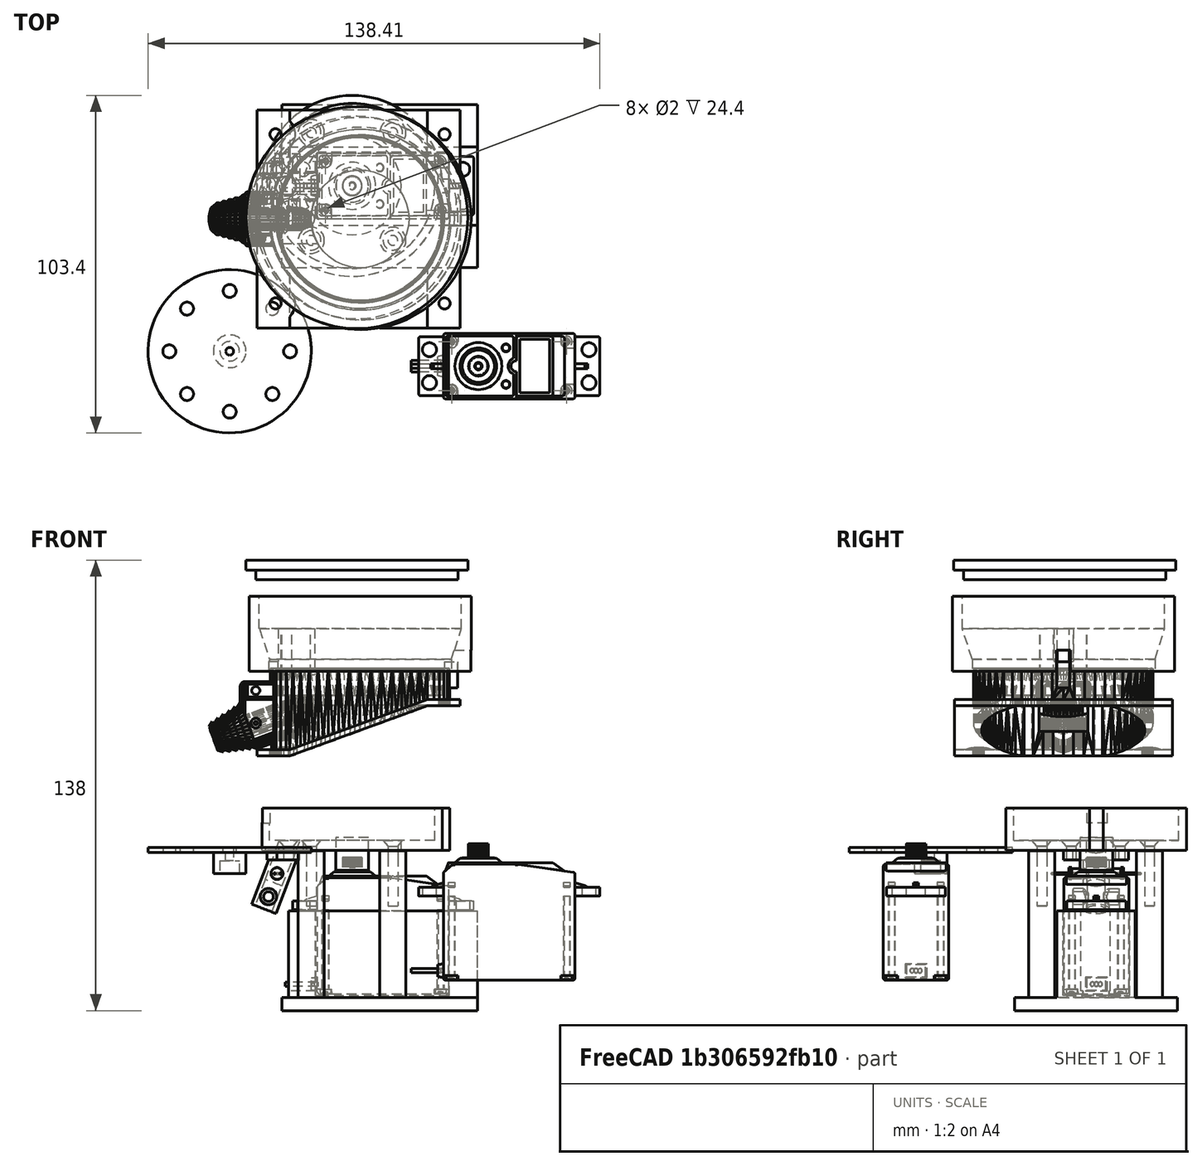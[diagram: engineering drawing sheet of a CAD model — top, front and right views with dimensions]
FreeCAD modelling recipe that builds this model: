
FCSTD DOCUMENT  (FreeCAD 0.21R33694 (Git))
Label: all_parts_chute_with_mount_v6
License: All rights reserved
LicenseURL: http://en.wikipedia.org/wiki/All_rights_reserved
objects: Part::Cylinder×34, Part::Cut×23, Part::MultiFuse×21, Part::Feature×18, Part::Box×11, Part::FeaturePython×5, Part::Cone×2, Sketcher::SketchObject×2, Part::Extrusion×2, Mesh::Feature×1, Part::Fillet×1, Part::Chamfer×1
note: 120 computed .brp shape members not serialized (recipe doc carries the construction recipe); baked Part::Feature solids carry a one-line shape summary decoded from their .brp

FEATURE [Part::Box] Box014  label="Cube014"
  AttacherType = Attacher::AttachEngine3D
  Height = 13
  Length = 4.2
  Placement = pos=(66.2,37.3,63.6) rot=(0,0,1;0rad)
  Width = 4.2
FEATURE [Part::Cylinder] Cylinder022
  Angle = 360
  AttacherType = Attacher::AttachEngine3D
  FirstAngle = 0
  Height = 20
  Placement = pos=(15.5,39.3,51.5) rot=(0,1,0;0.366519rad)
  Radius = 3
  SecondAngle = 0
FEATURE [Part::Box] Box015  label="Cube015"
  AttacherType = Attacher::AttachEngine3D
  Height = 10
  Length = 10
  Placement = pos=(7,36.6,72) rot=(0,0,1;0rad)
  Width = 6.2
FEATURE [Mesh::Feature] Base_V7  label="Base V7"
FEATURE [Part::Feature] Base_V7001_solid  label="hopper (Solid)"
  shape: bbox 76.98 x 66.8 x 28.84 mm, 5900 faces (baked)
FEATURE [Part::Feature] Shape001
  Placement = pos=(47,50.7,-44.8) rot=(0,0,1;3.14159rad)
  shape: bbox 57.75 x 20 x 41.74 mm, 378 faces, 4 solids (baked)
FEATURE [Part::Cylinder] cylinder010  label="servo_central_shaft"
  Angle = 360
  AttacherType = Attacher::AttachEngine3D
  FirstAngle = 0
  Height = 10
  Placement = pos=(37.55,50.7,-7) rot=(0,0,1;0rad)
  Radius = 5
  SecondAngle = 0
FEATURE [Part::Box] Box  label="Cube"
  AttacherType = Attacher::AttachEngine3D
  Height = 27.5
  Length = 58
  Placement = pos=(18,38.6,-47) rot=(0,0,1;0rad)
  Width = 24
FEATURE [Part::Box] Box016  label="Cube016"
  AttacherType = Attacher::AttachEngine3D
  Height = 29.5
  Length = 53
  Placement = pos=(13,46,-44) rot=(0,0,1;0rad)
  Width = 9
FEATURE [Part::Cut] Cut
  Base = -> Box
  Tool = -> Box016
FEATURE [Part::Box] Box017  label="Cube017"
  AttacherType = Attacher::AttachEngine3D
  Height = 29.5
  Length = 10
  Placement = pos=(17,46.6,-46) rot=(0,0,1;0rad)
  Width = 8
FEATURE [Part::Cut] Cut019
  Base = -> Cut
  Tool = -> Box017
FEATURE [Part::Box] Box018  label="Cube018"
  AttacherType = Attacher::AttachEngine3D
  Height = 27.5
  Length = 41
  Placement = pos=(0.5,50.4,-44.2) rot=(0,0,1;0rad)
  Width = 20.4
FEATURE [Part::Fillet] Fillet
  Base = -> Box018
  Edges = 4 edges r=1: [Edge1,Edge3,Edge5,Edge7]
  Placement = pos=(25.85,-9.87885,-1.16822) rot=(0,0,1;0rad)
FEATURE [Part::Cut] Cut020
  Base = -> Cut019
  Tool = -> Fillet
FEATURE [Part::Box] Box020  label="base_plate"
  AttacherType = Attacher::AttachEngine3D
  Height = 4
  Length = 60
  Placement = pos=(16,25.6,-50) rot=(0,0,1;0rad)
  Width = 50
FEATURE [Part::Feature] BOLTS_part  label="Hex socket countersunk head screw M3 20.0"
  Placement = pos=(25,67,2.1) rot=(0,1,0;3.14159rad)
  shape: bbox 6 x 6 x 20 mm, 12 faces (baked)
FEATURE [Part::Feature] BOLTS_part001  label="Hex socket countersunk head screw M3 20.001"
  Placement = pos=(50,67,2.1) rot=(0,1,0;3.14159rad)
  shape: bbox 6 x 6 x 20 mm, 12 faces (baked)
FEATURE [Part::Feature] BOLTS_part002  label="Hex socket countersunk head screw M3 20.002"
  Placement = pos=(50,34,2.1) rot=(0,1,0;3.14159rad)
  shape: bbox 6 x 6 x 20 mm, 12 faces (baked)
FEATURE [Part::Feature] BOLTS_part003  label="Hex socket countersunk head screw M3 20.003"
  Placement = pos=(25,34,2.1) rot=(0,1,0;3.14159rad)
  shape: bbox 6 x 6 x 20 mm, 12 faces (baked)
FEATURE [Part::Cylinder] Cylinder024
  Angle = 360
  AttacherType = Attacher::AttachEngine3D
  FirstAngle = 0
  Height = 48
  Placement = pos=(50,67,-49) rot=(0,0,1;0rad)
  Radius = 4
  SecondAngle = 0
FEATURE [Part::Cylinder] Cylinder025
  Angle = 360
  AttacherType = Attacher::AttachEngine3D
  FirstAngle = 0
  Height = 48
  Placement = pos=(25,34,-49) rot=(0,0,1;0rad)
  Radius = 4
  SecondAngle = 0
FEATURE [Part::Cylinder] Cylinder026
  Angle = 360
  AttacherType = Attacher::AttachEngine3D
  FirstAngle = 0
  Height = 48
  Placement = pos=(25,67,-49) rot=(0,0,1;0rad)
  Radius = 4
  SecondAngle = 0
FEATURE [Part::Cylinder] Cylinder027
  Angle = 360
  AttacherType = Attacher::AttachEngine3D
  FirstAngle = 0
  Height = 48
  Placement = pos=(50,34,-49) rot=(0,0,1;0rad)
  Radius = 4
  SecondAngle = 0
FEATURE [Part::Feature] Shape002  label="led2"
  Placement = pos=(14.5,42.3,-8) rot=(-1,0,0;1.5708rad)
  shape: bbox 3.686 x 11.4 x 3.686 mm, 26 faces, 3 solids (baked)
FEATURE [Part::Feature] Shape003  label="led1"
  Placement = pos=(14.5,59.1,-8) rot=(1,0,0;1.5708rad)
  shape: bbox 3.686 x 11.4 x 3.686 mm, 26 faces, 3 solids (baked)
FEATURE [Part::Feature] BOLTS_part004  label="Hex socket countersunk head screw M3 20.004"
  Placement = pos=(25,34,2.05) rot=(0,1,0;3.14159rad)
  shape: bbox 6 x 6 x 20 mm, 12 faces (baked)
FEATURE [Part::Feature] BOLTS_part005  label="Hex socket countersunk head screw M3 20.005"
  Placement = pos=(50,34,2.05) rot=(0,1,0;3.14159rad)
  shape: bbox 6 x 6 x 20 mm, 12 faces (baked)
FEATURE [Part::Feature] BOLTS_part006  label="Hex socket countersunk head screw M3 20.006"
  Placement = pos=(50,67,2.05) rot=(0,1,0;3.14159rad)
  shape: bbox 6 x 6 x 20 mm, 12 faces (baked)
FEATURE [Part::Feature] BOLTS_part007  label="Hex socket countersunk head screw M3 20.007"
  Placement = pos=(25,67,2.05) rot=(0,1,0;3.14159rad)
  shape: bbox 6 x 6 x 20 mm, 12 faces (baked)
FEATURE [Part::Cylinder] Cylinder032
  Angle = 360
  AttacherType = Attacher::AttachEngine3D
  FirstAngle = 0
  Height = 48
  Placement = pos=(50,67,-43) rot=(0,0,1;0rad)
  Radius = 1.4
  SecondAngle = 0
FEATURE [Part::Cylinder] Cylinder033
  Angle = 360
  AttacherType = Attacher::AttachEngine3D
  FirstAngle = 0
  Height = 48
  Placement = pos=(25,34,-43) rot=(0,0,1;0rad)
  Radius = 1.4
  SecondAngle = 0
FEATURE [Part::Cylinder] Cylinder034
  Angle = 360
  AttacherType = Attacher::AttachEngine3D
  FirstAngle = 0
  Height = 48
  Placement = pos=(25,67,-42) rot=(0,0,1;0rad)
  Radius = 1.4
  SecondAngle = 0
FEATURE [Part::Cylinder] Cylinder035
  Angle = 360
  AttacherType = Attacher::AttachEngine3D
  FirstAngle = 0
  Height = 48
  Placement = pos=(50,34,-43) rot=(0,0,1;0rad)
  Radius = 1.4
  SecondAngle = 0
FEATURE [Part::Cut] Cut030
  Base = -> Cylinder024
  Tool = -> BOLTS_part006
FEATURE [Part::Cut] Cut031
  Base = -> Cylinder025
  Tool = -> BOLTS_part004
FEATURE [Part::Cut] Cut032
  Base = -> Cylinder026
  Tool = -> BOLTS_part007
FEATURE [Part::Cut] Cut033
  Base = -> Cylinder027
  Tool = -> BOLTS_part005
FEATURE [Part::MultiFuse] Fusion011  label="motor_holder"
  Shapes = -> [Cut020,Cut030,Cut031,Cut032,Cut033,Box020]
FEATURE [Part::Cylinder] Cylinder039
  Angle = 360
  AttacherType = Attacher::AttachEngine3D
  FirstAngle = 0
  Height = 21
  Placement = pos=(0,10,4) rot=(1,0,0;1.5708rad)
  Radius = 1.5
  SecondAngle = 0
FEATURE [Part::FeaturePython] Tube003  # WARN: FeaturePython — macro-defined, semantics opaque (R4)
  AttacherType = Attacher::AttachEngine3D
  Height = 5
  InnerRadius = 1.5
  OuterRadius = 2.5
  Placement = pos=(0,2.05,4) rot=(-1,0,0;1.5708rad)
FEATURE [Part::FeaturePython] Tube004  # WARN: FeaturePython — macro-defined, semantics opaque (R4)
  AttacherType = Attacher::AttachEngine3D
  Height = 5
  InnerRadius = 1.5
  OuterRadius = 2.5
  Placement = pos=(0,-2.05,4) rot=(1,0,0;1.5708rad)
FEATURE [Part::Box] Box021  label="Cube019"
  AttacherType = Attacher::AttachEngine3D
  Height = 10
  Length = 20
  Placement = pos=(1.17,-11.94,17.9) rot=(0,0,1;0rad)
  Width = 24
FEATURE [Part::FeaturePython] Tube001  # WARN: FeaturePython — macro-defined, semantics opaque (R4)
  AttacherType = Attacher::AttachEngine3D
  Height = 3
  InnerRadius = 15
  OuterRadius = 27.7
  Placement = pos=(40.45,39.4,63.6) rot=(0,0,1;0rad)
FEATURE [Part::FeaturePython] Tube002  # WARN: FeaturePython — macro-defined, semantics opaque (R4)
  AttacherType = Attacher::AttachEngine3D
  Height = 13
  InnerRadius = 25.3
  OuterRadius = 27.7
  Placement = pos=(40.45,39.4,63.6) rot=(0,0,1;0rad)
FEATURE [Part::MultiFuse] Fusion009
  Shapes = -> [Box014,Tube001,Tube002]
FEATURE [Part::Cut] Cut014  label="cut"
  Base = -> Fusion009
  Tool = -> Cylinder022
FEATURE [Part::Cut] Cut036
  Base = -> Cut014
  Placement = pos=(-2.9,11.3,-64.5) rot=(0,0,1;0rad)
  Tool = -> Box015
FEATURE [Part::MultiFuse] Fusion
  Shapes = -> [BOLTS_part003,Cylinder033]
FEATURE [Part::MultiFuse] Fusion013
  Shapes = -> [BOLTS_part002,Cylinder035]
FEATURE [Part::MultiFuse] Fusion014
  Shapes = -> [BOLTS_part001,Cylinder032]
FEATURE [Part::MultiFuse] Fusion015
  Shapes = -> [BOLTS_part,Cylinder034]
FEATURE [Part::Cut] Cut037
  Base = -> Cut036
  Tool = -> Fusion
FEATURE [Part::Cut] Cut038
  Base = -> Cut037
  Tool = -> Fusion013
FEATURE [Part::Cut] Cut039
  Base = -> Cut038
  Tool = -> Fusion015
FEATURE [Part::Cut] Cut040
  Base = -> Cut039
  Tool = -> Fusion014
FEATURE [Part::Feature] BOLTS_part009  label="Hex socket countersunk head screw M3 20.008"
  Placement = pos=(50,34,2.1) rot=(0,1,0;3.14159rad)
  shape: bbox 6 x 6 x 20 mm, 12 faces (baked)
FEATURE [Part::Cylinder] Cylinder040
  Angle = 360
  AttacherType = Attacher::AttachEngine3D
  FirstAngle = 0
  Height = 48
  Placement = pos=(50,34,-43) rot=(0,0,1;0rad)
  Radius = 1.4
  SecondAngle = 0
FEATURE [Part::MultiFuse] Fusion016
  Placement = pos=(-32,9,0) rot=(0,0,1;0rad)
  Shapes = -> [BOLTS_part009,Cylinder040]
FEATURE [Part::Feature] BOLTS_part010  label="Hex socket countersunk head screw M3 20.009"
  Placement = pos=(50,34,2.1) rot=(0,1,0;3.14159rad)
  shape: bbox 6 x 6 x 20 mm, 12 faces (baked)
FEATURE [Part::Cylinder] Cylinder041
  Angle = 360
  AttacherType = Attacher::AttachEngine3D
  FirstAngle = 0
  Height = 48
  Placement = pos=(50,34,-43) rot=(0,0,1;0rad)
  Radius = 1.4
  SecondAngle = 0
FEATURE [Part::MultiFuse] Fusion017
  Placement = pos=(-32,24,0) rot=(0,0,1;0rad)
  Shapes = -> [BOLTS_part010,Cylinder041]
FEATURE [Part::Box] Box022  label="Cube020"
  AttacherType = Attacher::AttachEngine3D
  Height = 3
  Length = 10
  Placement = pos=(3,-10,15) rot=(0,0,1;0rad)
  Width = 20
FEATURE [Part::Cylinder] Cylinder
  Angle = 360
  AttacherType = Attacher::AttachEngine3D
  FirstAngle = 0
  Height = 18
  Radius = 4
  SecondAngle = 0
FEATURE [Part::Cut] Cut043
  Base = -> Cylinder
  Tool = -> Cylinder039
FEATURE [Part::MultiFuse] Fusion018
  Placement = pos=(2,0,0) rot=(0,1,0;0.366519rad)
  Shapes = -> [Tube003,Tube004,Cut043]
FEATURE [Part::MultiFuse] Fusion019
  Shapes = -> [Fusion018,Box022]
FEATURE [Part::Feature] BOLTS_part011  label="Hex socket countersunk head screw M3 20.010"
  Placement = pos=(50,34,2.1) rot=(0,1,0;3.14159rad)
  shape: bbox 6 x 6 x 20 mm, 12 faces (baked)
FEATURE [Part::Cylinder] Cylinder044
  Angle = 360
  AttacherType = Attacher::AttachEngine3D
  FirstAngle = 0
  Height = 48
  Placement = pos=(50,34,-43) rot=(0,0,1;0rad)
  Radius = 1.4
  SecondAngle = 0
FEATURE [Part::MultiFuse] Fusion021
  Placement = pos=(-32,9,0) rot=(0,0,1;0rad)
  Shapes = -> [BOLTS_part011,Cylinder044]
FEATURE [Part::Feature] BOLTS_part012  label="Hex socket countersunk head screw M3 20.011"
  Placement = pos=(50,34,2.1) rot=(0,1,0;3.14159rad)
  shape: bbox 6 x 6 x 20 mm, 12 faces (baked)
FEATURE [Part::Cylinder] Cylinder045
  Angle = 360
  AttacherType = Attacher::AttachEngine3D
  FirstAngle = 0
  Height = 48
  Placement = pos=(50,34,-43) rot=(0,0,1;0rad)
  Radius = 1.4
  SecondAngle = 0
FEATURE [Part::MultiFuse] Fusion022
  Placement = pos=(-32,24,0) rot=(0,0,1;0rad)
  Shapes = -> [BOLTS_part012,Cylinder045]
FEATURE [Part::Cut] Cut047
  Base = -> Cut040
  Tool = -> Fusion016
FEATURE [Part::Cut] Cut048  label="base"
  Base = -> Cut047
  Tool = -> Fusion017
FEATURE [Part::Feature] Shape004
  Placement = pos=(85.6641,-4.55315,-40.6487) rot=(0,0,1;3.14159rad)
  shape: bbox 57.75 x 20 x 41.74 mm, 378 faces, 4 solids (baked)
FEATURE [Part::Box] Box012  label="Cube012"
  AttacherType = Attacher::AttachEngine3D
  Height = 10
  Length = 10
  Placement = pos=(7,36.17,76) rot=(0,0,1;0rad)
  Width = 6
FEATURE [Part::Box] Box013  label="Cube013"
  AttacherType = Attacher::AttachEngine3D
  Height = 10
  Length = 14
  Placement = pos=(64,38.5,50.5) rot=(0,0,1;0rad)
  Width = 4.3
FEATURE [Part::Cone] Cone
  Angle = 360
  AttacherType = Attacher::AttachEngine3D
  Height = 14
  Placement = pos=(40,40.65,53) rot=(0,0,1;0rad)
  Radius1 = 26.5
  Radius2 = 31
FEATURE [Part::Cylinder] Cylinder019
  Angle = 360
  AttacherType = Attacher::AttachEngine3D
  FirstAngle = 0
  Height = 13
  Placement = pos=(40,40.65,54) rot=(0,0,1;0rad)
  Radius = 34
  SecondAngle = 0
FEATURE [Part::Cylinder] Cylinder020
  Angle = 360
  AttacherType = Attacher::AttachEngine3D
  FirstAngle = 0
  Height = 13
  Placement = pos=(40,39.2,54) rot=(0,0,1;0rad)
  Radius = 25
  SecondAngle = 0
FEATURE [Part::Cylinder] Cylinder021
  Angle = 360
  AttacherType = Attacher::AttachEngine3D
  FirstAngle = 0
  Height = 4
  Placement = pos=(40,40.65,54) rot=(0,0,1;0rad)
  Radius = 28
  SecondAngle = 0
FEATURE [Sketcher::SketchObject] Sketch001
  FullyConstrained = true
  MapMode = 2
  Placement = pos=(0,5,65) rot=(0,0,1;0rad)
  sketch-geometry (8):
    g0: ArcOfCircle CenterX=20.555 CenterY=41.4363 CenterZ=0 NormalX=0 NormalY=0 NormalZ=1 AngleXU=0 Radius=4.5 StartAngle=3.17145 EndAngle=4.38602
    g1: ArcOfCircle CenterX=24.0176 CenterY=34.022 CenterZ=0 NormalX=0 NormalY=0 NormalZ=1 AngleXU=0 Radius=2 StartAngle=5.10518 EndAngle=7.46119
    g2: ArcOfCircle CenterX=20.5312 CenterY=26.882 CenterZ=0 NormalX=0 NormalY=0 NormalZ=1 AngleXU=0 Radius=4.5 StartAngle=1.8916 EndAngle=3.11914
    g3: LineSegment StartX=19.1123 StartY=31.1525 StartZ=0 EndX=24.7831 EndY=32.1743 EndZ=0
    g4: LineSegment StartX=19.1123 StartY=37.1738 StartZ=0 EndX=24.7831 EndY=35.8697 EndZ=0
    g5: LineSegment StartX=16.057 StartY=41.302 StartZ=0 EndX=15.8089 EndY=41.3763 EndZ=0
    g6: LineSegment StartX=15.8133 StartY=26.9187 StartZ=0 EndX=16.0324 EndY=26.9831 EndZ=0
    g7: ArcOfCircle CenterX=39.7432 CenterY=34.1548 CenterZ=0 NormalX=0 NormalY=0 NormalZ=1 AngleXU=0 Radius=25 StartAngle=2.84856 EndAngle=3.43524
  constraints (28):
    c: Coincident(g3,g2)
    c: Coincident(g3,g1)
    c: Coincident(g4,g0)
    c: Coincident(g4,g1)
    c: Coincident(g5,g0)
    c: Coincident(g6,g2)
    c: Coincident(g7,g6)
    c: Coincident(g7,g5)
    c: Radius(g2) = 4.5
    c: Radius(g0) = 4.5
    c: Radius(g1) = 2
    c: Radius(g7) = 25
    c: DistanceX(g5) = 15.8089
    c: DistanceY(g5) = 41.3763
    c: DistanceX(g2) = 16.0324
    c: DistanceY(g2) = 26.9831
    c: DistanceX(g3) = 19.1123
    c: DistanceY(g3) = 31.1525
    c: DistanceX(g2,g0) = 0
    c: DistanceX(g3,g1) = 0
    c: DistanceX(g1) = 24.7831
    c: DistanceY(g1) = 32.1743
    c: DistanceX(g5) = 16.057
    c: DistanceY(g5) = 41.302
    c: DistanceX(g7) = 15.8133
    c: DistanceY(g7) = 26.9187
    c: DistanceY(g1) = 35.8697
    c: DistanceY(g0) = 37.1738
FEATURE [Part::Extrusion] Extrude001
  Base = -> Sketch001
  Dir = (0,0,1)
  DirMode = 2
  FaceMakerClass = Part::FaceMakerBullseye
  LengthFwd = 14
  LengthRev = 0
  Placement = pos=(0,0,7) rot=(0,0,1;0rad)
  Solid = true
  Symmetric = false
FEATURE [Part::MultiFuse] Fusion006  label="pellet_sorter"
  Placement = pos=(0,1.5,-19) rot=(0,0,1;0rad)
  Shapes = -> [Box012,Extrude001]
FEATURE [Part::FeaturePython] Tube  # WARN: FeaturePython — macro-defined, semantics opaque (R4)
  AttacherType = Attacher::AttachEngine3D
  Height = 23
  InnerRadius = 31
  OuterRadius = 34
  Placement = pos=(40,40.65,54) rot=(0,0,1;0rad)
FEATURE [Part::MultiFuse] Fusion010
  Shapes = -> [Tube,Cylinder019,Cylinder020]
FEATURE [Part::Cut] Cut015
  Base = -> Fusion010
  Tool = -> Cone
FEATURE [Part::Cut] Cut016
  Base = -> Cut015
  Tool = -> Cylinder021
FEATURE [Part::MultiFuse] Fusion024
  Shapes = -> [Fusion006,Cut016]
FEATURE [Part::Cut] Cut017  label="lid"
  Base = -> Fusion024
  Tool = -> Box013
FEATURE [Part::Cylinder] Cylinder047
  Angle = 360
  AttacherType = Attacher::AttachEngine3D
  FirstAngle = 0
  Height = 3
  Radius = 34
  SecondAngle = 0
FEATURE [Part::Cylinder] Cylinder048
  Angle = 360
  AttacherType = Attacher::AttachEngine3D
  FirstAngle = 0
  Height = 6
  Radius = 31
  SecondAngle = 0
FEATURE [Part::MultiFuse] Fusion025  label="cap"
  Placement = pos=(39,41,88) rot=(1,0,0;3.14159rad)
  Shapes = -> [Cylinder047,Cylinder048]
FEATURE [Part::Cylinder] cylinder012
  Angle = 360
  AttacherType = Attacher::AttachEngine3D
  FirstAngle = 0
  Height = 1.5
  Radius = 25
  SecondAngle = 0
FEATURE [Part::Cylinder] cylinder013
  Angle = 360
  AttacherType = Attacher::AttachEngine3D
  FirstAngle = 0
  Height = 5
  Placement = pos=(18.5,0,0) rot=(0,0,1;0rad)
  Radius = 2
  SecondAngle = 0
FEATURE [Part::Cylinder] cylinder014
  Angle = 360
  AttacherType = Attacher::AttachEngine3D
  FirstAngle = 0
  Height = 5
  Placement = pos=(13.0815,13.0815,0) rot=(0,0,1;0.785398rad)
  Radius = 2
  SecondAngle = 0
FEATURE [Part::Cylinder] cylinder015
  Angle = 360
  AttacherType = Attacher::AttachEngine3D
  FirstAngle = 0
  Height = 5
  Placement = pos=(0,18.5,0) rot=(0,0,1;1.5708rad)
  Radius = 2
  SecondAngle = 0
FEATURE [Part::Cylinder] cylinder016
  Angle = 360
  AttacherType = Attacher::AttachEngine3D
  FirstAngle = 0
  Height = 5
  Placement = pos=(-13.0815,13.0815,0) rot=(0,0,1;2.35619rad)
  Radius = 2
  SecondAngle = 0
FEATURE [Part::Cylinder] cylinder017
  Angle = 360
  AttacherType = Attacher::AttachEngine3D
  FirstAngle = 0
  Height = 5
  Placement = pos=(-18.5,2e-15,0) rot=(0,0,1;3.14159rad)
  Radius = 2
  SecondAngle = 0
FEATURE [Part::Cylinder] cylinder018
  Angle = 360
  AttacherType = Attacher::AttachEngine3D
  FirstAngle = 0
  Height = 5
  Placement = pos=(-13.0815,-13.0815,0) rot=(0,0,1;3.92699rad)
  Radius = 2
  SecondAngle = 0
FEATURE [Part::Cylinder] cylinder019
  Angle = 360
  AttacherType = Attacher::AttachEngine3D
  FirstAngle = 0
  Height = 5
  Placement = pos=(0,-18.5,0) rot=(0,0,-1;1.5708rad)
  Radius = 2
  SecondAngle = 0
FEATURE [Part::Cylinder] cylinder020
  Angle = 360
  AttacherType = Attacher::AttachEngine3D
  FirstAngle = 0
  Height = 5
  Placement = pos=(13.0815,-13.0815,0) rot=(0,0,-1;0.785398rad)
  Radius = 2
  SecondAngle = 0
FEATURE [Part::MultiFuse] Group001
  Placement = pos=(0,0,-1) rot=(0,0,1;0rad)
  Shapes = -> [cylinder013,cylinder014,cylinder015,cylinder016,cylinder017,cylinder018,cylinder019,cylinder020]
FEATURE [Part::Feature] Shape005
  Placement = pos=(85.6641,-4.55315,-40.6487) rot=(0,0,1;3.14159rad)
  shape: bbox 57.75 x 20 x 41.74 mm, 378 faces, 4 solids (baked)
FEATURE [Part::Cylinder] cylinder021  label="servo_central_shaft002"
  Angle = 360
  AttacherType = Attacher::AttachEngine3D
  FirstAngle = 0
  Height = 8
  Radius = 5
  SecondAngle = 0
FEATURE [Sketcher::SketchObject] Sketch002
  FullyConstrained = false
  MapMode = 5
  Placement = pos=(85.6641,-4.55315,1.09128) rot=(0,0,1;3.14159rad)
  Support = -> [Shape005]
  sketch-geometry (1):
    g0: Circle CenterX=9.4502 CenterY=-0.000218 CenterZ=0 NormalX=0 NormalY=0 NormalZ=1 AngleXU=0 Radius=3
  constraints (1):
    c: Radius(g0) = 3
FEATURE [Part::Extrusion] Extrude002
  Base = -> Sketch002
  Dir = (0,0,1)
  DirMode = 2
  FaceMakerClass = Part::FaceMakerBullseye
  LengthFwd = 6
  LengthRev = 0
  Placement = pos=(-76.21,4.55,3) rot=(0,0,1;0rad)
  Solid = true
  Symmetric = false
FEATURE [Part::Cylinder] Cylinder049
  Angle = 360
  AttacherType = Attacher::AttachEngine3D
  FirstAngle = 0
  Height = 19
  Placement = pos=(0,0,-1) rot=(0,0,1;0rad)
  Radius = 1.2
  SecondAngle = 0
FEATURE [Part::MultiFuse] Fusion026
  Shapes = -> [Group001,Extrude002,Cylinder049]
FEATURE [Part::MultiFuse] Fusion027
  Shapes = -> [cylinder012,cylinder021]
FEATURE [Part::Cut] Cut050  label="rotor001"
  Base = -> Fusion027
  Placement = pos=(0,0,0) rot=(1,0,0;3.14159rad)
  Tool = -> Fusion026
FEATURE [Part::Cone] Cone001
  Angle = 360
  AttacherType = Attacher::AttachEngine3D
  Height = 11
  Placement = pos=(0,-29,0) rot=(0,0,1;0rad)
  Radius1 = 2.75
  Radius2 = 3
FEATURE [Part::Cylinder] Cylinder050
  Angle = 360
  AttacherType = Attacher::AttachEngine3D
  FirstAngle = 0
  Height = 10
  Placement = pos=(0,-29,-10) rot=(0,0,1;0rad)
  Radius = 2.75
  SecondAngle = 0
FEATURE [Part::Cylinder] Cylinder051
  Angle = 360
  AttacherType = Attacher::AttachEngine3D
  FirstAngle = 0
  Height = 14
  Placement = pos=(0,-29,11) rot=(0,0,1;0rad)
  Radius = 3
  SecondAngle = 0
FEATURE [Part::MultiFuse] Fusion028
  Placement = pos=(5,29,8) rot=(0,1,0;0.366519rad)
  Shapes = -> [Cone001,Cylinder050,Cylinder051]
FEATURE [Part::MultiFuse] Fusion020
  Shapes = -> [Box021,Fusion028]
FEATURE [Part::Cut] Cut044  label="foodchute"
  Base = -> Fusion019
  Placement = pos=(8.45427,50.6,-18.8) rot=(0,0,1;0rad)
  Tool = -> Fusion020
FEATURE [Part::Chamfer] Chamfer
  Base = -> Cut044
  Edges = 2 edges r=3: [Edge1,Edge3]
FEATURE [Part::Cut] Cut045
  Base = -> Chamfer
  Tool = -> Fusion021
FEATURE [Part::Cut] Cut046  label="chute_with_mount"
  Base = -> Cut045
  Tool = -> Fusion022
